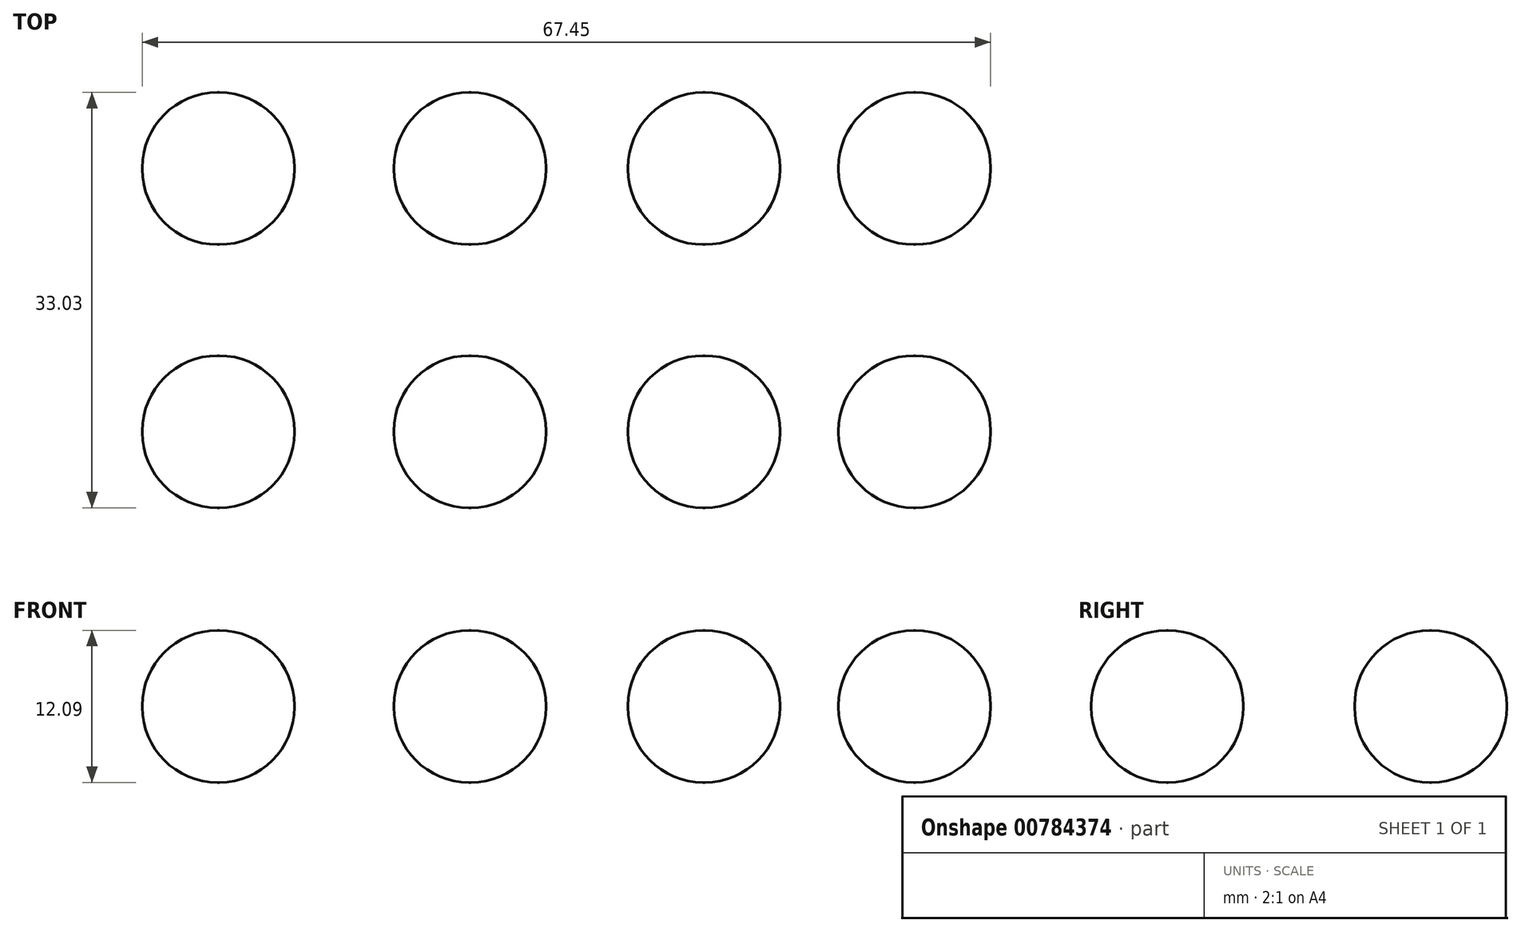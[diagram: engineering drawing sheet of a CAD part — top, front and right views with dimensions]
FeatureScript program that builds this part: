
annotation { "Feature Type Name" : "Feature", "Feature Type Description" : "" }
export const myFeature = defineFeature(function(context is Context, id is Id, definition is map)
    precondition{}
    {
        {
            var Q0;
            Q0=qCreatedBy(makeId("Top.planeOp"),FACE);
            var sketch = newSketch(context, id + "F0", { "sketchPlane" : qUnion([Q0])});
            skLineSegment(sketch, "E0.bottom", {"start": v(-61.29, 39.2) * mm, "end": v(-49.2, 39.2) * mm});
            skLineSegment(sketch, "E0.top", {"start": v(-61.29, 27.1) * mm, "end": v(-49.2, 27.1) * mm});
            skLineSegment(sketch, "E0.left", {"start": v(-61.29, 39.2) * mm, "end": v(-61.29, 27.1) * mm});
            skLineSegment(sketch, "E0.right", {"start": v(-49.2, 39.2) * mm, "end": v(-49.2, 27.1) * mm});
            skLineSegment(sketch, "E1.bottom", {"start": v(-61.29, 18.26) * mm, "end": v(-49.2, 18.26) * mm});
            skLineSegment(sketch, "E1.top", {"start": v(-61.29, 6.16) * mm, "end": v(-49.2, 6.16) * mm});
            skLineSegment(sketch, "E1.left", {"start": v(-61.29, 18.26) * mm, "end": v(-61.29, 6.16) * mm});
            skLineSegment(sketch, "E1.right", {"start": v(-49.2, 18.26) * mm, "end": v(-49.2, 6.16) * mm});
            skLineSegment(sketch, "E2.bottom", {"start": v(-41.28, 39.2) * mm, "end": v(-29.19, 39.2) * mm});
            skLineSegment(sketch, "E2.top", {"start": v(-41.28, 27.1) * mm, "end": v(-29.19, 27.1) * mm});
            skLineSegment(sketch, "E2.left", {"start": v(-41.28, 39.2) * mm, "end": v(-41.28, 27.1) * mm});
            skLineSegment(sketch, "E2.right", {"start": v(-29.19, 39.2) * mm, "end": v(-29.19, 27.1) * mm});
            skLineSegment(sketch, "E3.bottom", {"start": v(-41.28, 18.26) * mm, "end": v(-29.19, 18.26) * mm});
            skLineSegment(sketch, "E3.top", {"start": v(-41.28, 6.16) * mm, "end": v(-29.19, 6.16) * mm});
            skLineSegment(sketch, "E3.left", {"start": v(-41.28, 18.26) * mm, "end": v(-41.28, 6.16) * mm});
            skLineSegment(sketch, "E3.right", {"start": v(-29.19, 18.26) * mm, "end": v(-29.19, 6.16) * mm});
            skLineSegment(sketch, "E4.bottom", {"start": v(-22.68, 39.2) * mm, "end": v(-10.58, 39.2) * mm});
            skLineSegment(sketch, "E4.top", {"start": v(-22.68, 27.1) * mm, "end": v(-10.58, 27.1) * mm});
            skLineSegment(sketch, "E4.left", {"start": v(-22.68, 39.2) * mm, "end": v(-22.68, 27.1) * mm});
            skLineSegment(sketch, "E4.right", {"start": v(-10.58, 39.2) * mm, "end": v(-10.58, 27.1) * mm});
            skLineSegment(sketch, "E5.bottom", {"start": v(-5.93, 39.2) * mm, "end": v(6.16, 39.2) * mm});
            skLineSegment(sketch, "E5.top", {"start": v(-5.93, 27.1) * mm, "end": v(6.16, 27.1) * mm});
            skLineSegment(sketch, "E5.left", {"start": v(-5.93, 39.2) * mm, "end": v(-5.93, 27.1) * mm});
            skLineSegment(sketch, "E5.right", {"start": v(6.16, 39.2) * mm, "end": v(6.16, 27.1) * mm});
            skLineSegment(sketch, "E6.bottom", {"start": v(-22.68, 18.26) * mm, "end": v(-10.58, 18.26) * mm});
            skLineSegment(sketch, "E6.top", {"start": v(-22.68, 6.16) * mm, "end": v(-10.58, 6.16) * mm});
            skLineSegment(sketch, "E6.left", {"start": v(-22.68, 18.26) * mm, "end": v(-22.68, 6.16) * mm});
            skLineSegment(sketch, "E6.right", {"start": v(-10.58, 18.26) * mm, "end": v(-10.58, 6.16) * mm});
            skLineSegment(sketch, "E7.bottom", {"start": v(-5.93, 18.26) * mm, "end": v(6.16, 18.26) * mm});
            skLineSegment(sketch, "E7.top", {"start": v(-5.93, 6.16) * mm, "end": v(6.16, 6.16) * mm});
            skLineSegment(sketch, "E7.left", {"start": v(-5.93, 18.26) * mm, "end": v(-5.93, 6.16) * mm});
            skLineSegment(sketch, "E7.right", {"start": v(6.16, 18.26) * mm, "end": v(6.16, 6.16) * mm});
            skSolve(sketch);
        }
        {
            var Q0;
            Q0 = qSketchRegion(id + "F0", true);
            extrude(context, id + "F1", {"entities" : qUnion([Q0]), "depth" : 12.1 * mm, "offsetDistance" : 25.4 * mm});
        }
        {
            var Q0;
            Q0=makeQuery(id+"F1.opExtrude","CAP_EDGE",EDGE,{"disambiguationData":[OSD([sQuery(id+"F0.wireOp",EDGE,"E0.left")])],"isStart":false});
            var Q1;
            Q1=makeQuery(id+"F1.opExtrude","CAP_EDGE",EDGE,{"disambiguationData":[OSD([sQuery(id+"F0.wireOp",EDGE,"E0.top")])],"isStart":false});
            var Q2;
            Q2=makeQuery(id+"F1.opExtrude","CAP_EDGE",EDGE,{"disambiguationData":[OSD([sQuery(id+"F0.wireOp",EDGE,"E0.bottom")])],"isStart":false});
            var Q3;
            Q3=makeQuery(id+"F1.opExtrude","CAP_EDGE",EDGE,{"disambiguationData":[OSD([sQuery(id+"F0.wireOp",EDGE,"E0.right")])],"isStart":false});
            var Q4;
            Q4=makeQuery(id+"F1.opExtrude","CAP_EDGE",EDGE,{"disambiguationData":[OSD([sQuery(id+"F0.wireOp",EDGE,"E2.left")])],"isStart":false});
            var Q5;
            Q5=makeQuery(id+"F1.opExtrude","CAP_EDGE",EDGE,{"disambiguationData":[OSD([sQuery(id+"F0.wireOp",EDGE,"E2.top")])],"isStart":false});
            var Q6;
            Q6=makeQuery(id+"F1.opExtrude","CAP_EDGE",EDGE,{"disambiguationData":[OSD([sQuery(id+"F0.wireOp",EDGE,"E2.right")])],"isStart":false});
            var Q7;
            Q7=makeQuery(id+"F1.opExtrude","CAP_EDGE",EDGE,{"disambiguationData":[OSD([sQuery(id+"F0.wireOp",EDGE,"E2.bottom")])],"isStart":false});
            var Q8;
            Q8=makeQuery(id+"F1.opExtrude","CAP_EDGE",EDGE,{"disambiguationData":[OSD([sQuery(id+"F0.wireOp",EDGE,"E4.bottom")])],"isStart":false});
            var Q9;
            Q9=makeQuery(id+"F1.opExtrude","CAP_EDGE",EDGE,{"disambiguationData":[OSD([sQuery(id+"F0.wireOp",EDGE,"E4.left")])],"isStart":false});
            var Q10;
            Q10=makeQuery(id+"F1.opExtrude","CAP_EDGE",EDGE,{"disambiguationData":[OSD([sQuery(id+"F0.wireOp",EDGE,"E4.top")])],"isStart":false});
            var Q11;
            Q11=makeQuery(id+"F1.opExtrude","CAP_EDGE",EDGE,{"disambiguationData":[OSD([sQuery(id+"F0.wireOp",EDGE,"E4.right")])],"isStart":false});
            var Q12;
            Q12=makeQuery(id+"F1.opExtrude","CAP_EDGE",EDGE,{"disambiguationData":[OSD([sQuery(id+"F0.wireOp",EDGE,"E5.left")])],"isStart":false});
            var Q13;
            Q13=makeQuery(id+"F1.opExtrude","CAP_EDGE",EDGE,{"disambiguationData":[OSD([sQuery(id+"F0.wireOp",EDGE,"E5.bottom")])],"isStart":false});
            var Q14;
            Q14=makeQuery(id+"F1.opExtrude","CAP_EDGE",EDGE,{"disambiguationData":[OSD([sQuery(id+"F0.wireOp",EDGE,"E5.right")])],"isStart":false});
            var Q15;
            Q15=makeQuery(id+"F1.opExtrude","CAP_EDGE",EDGE,{"disambiguationData":[OSD([sQuery(id+"F0.wireOp",EDGE,"E5.top")])],"isStart":false});
            var Q16;
            Q16=makeQuery(id+"F1.opExtrude","CAP_EDGE",EDGE,{"disambiguationData":[OSD([sQuery(id+"F0.wireOp",EDGE,"E7.bottom")])],"isStart":false});
            var Q17;
            Q17=makeQuery(id+"F1.opExtrude","CAP_EDGE",EDGE,{"disambiguationData":[OSD([sQuery(id+"F0.wireOp",EDGE,"E7.right")])],"isStart":false});
            var Q18;
            Q18=makeQuery(id+"F1.opExtrude","CAP_EDGE",EDGE,{"disambiguationData":[OSD([sQuery(id+"F0.wireOp",EDGE,"E7.top")])],"isStart":false});
            var Q19;
            Q19=makeQuery(id+"F1.opExtrude","CAP_EDGE",EDGE,{"disambiguationData":[OSD([sQuery(id+"F0.wireOp",EDGE,"E7.left")])],"isStart":false});
            var Q20;
            Q20=makeQuery(id+"F1.opExtrude","CAP_EDGE",EDGE,{"disambiguationData":[OSD([sQuery(id+"F0.wireOp",EDGE,"E6.right")])],"isStart":false});
            var Q21;
            Q21=makeQuery(id+"F1.opExtrude","CAP_EDGE",EDGE,{"disambiguationData":[OSD([sQuery(id+"F0.wireOp",EDGE,"E6.top")])],"isStart":false});
            var Q22;
            Q22=makeQuery(id+"F1.opExtrude","CAP_EDGE",EDGE,{"disambiguationData":[OSD([sQuery(id+"F0.wireOp",EDGE,"E6.bottom")])],"isStart":false});
            var Q23;
            Q23=makeQuery(id+"F1.opExtrude","CAP_EDGE",EDGE,{"disambiguationData":[OSD([sQuery(id+"F0.wireOp",EDGE,"E6.left")])],"isStart":false});
            var Q24;
            Q24=makeQuery(id+"F1.opExtrude","CAP_EDGE",EDGE,{"disambiguationData":[OSD([sQuery(id+"F0.wireOp",EDGE,"E3.top")])],"isStart":false});
            var Q25;
            Q25=makeQuery(id+"F1.opExtrude","CAP_EDGE",EDGE,{"disambiguationData":[OSD([sQuery(id+"F0.wireOp",EDGE,"E3.right")])],"isStart":false});
            var Q26;
            Q26=makeQuery(id+"F1.opExtrude","CAP_EDGE",EDGE,{"disambiguationData":[OSD([sQuery(id+"F0.wireOp",EDGE,"E3.bottom")])],"isStart":false});
            var Q27;
            Q27=makeQuery(id+"F1.opExtrude","CAP_EDGE",EDGE,{"disambiguationData":[OSD([sQuery(id+"F0.wireOp",EDGE,"E3.left")])],"isStart":false});
            var Q28;
            Q28=makeQuery(id+"F1.opExtrude","CAP_EDGE",EDGE,{"disambiguationData":[OSD([sQuery(id+"F0.wireOp",EDGE,"E1.right")])],"isStart":false});
            var Q29;
            Q29=makeQuery(id+"F1.opExtrude","CAP_EDGE",EDGE,{"disambiguationData":[OSD([sQuery(id+"F0.wireOp",EDGE,"E1.top")])],"isStart":false});
            var Q30;
            Q30=makeQuery(id+"F1.opExtrude","CAP_EDGE",EDGE,{"disambiguationData":[OSD([sQuery(id+"F0.wireOp",EDGE,"E1.left")])],"isStart":false});
            var Q31;
            Q31=makeQuery(id+"F1.opExtrude","CAP_EDGE",EDGE,{"disambiguationData":[OSD([sQuery(id+"F0.wireOp",EDGE,"E1.bottom")])],"isStart":false});
            var Q32;
            Q32=makeQuery(id+"F1.opExtrude","SWEPT_EDGE",EDGE,{"disambiguationData":[OSD([sQuery(id+"F0.wireOp",EDGE,"E7.top"),sQuery(id+"F0.wireOp",EDGE,"E7.right")])]});
            var Q33;
            Q33=makeQuery(id+"F1.opExtrude","SWEPT_EDGE",EDGE,{"disambiguationData":[OSD([sQuery(id+"F0.wireOp",EDGE,"E7.top"),sQuery(id+"F0.wireOp",EDGE,"E7.left")])]});
            var Q34;
            Q34=makeQuery(id+"F1.opExtrude","SWEPT_EDGE",EDGE,{"disambiguationData":[OSD([sQuery(id+"F0.wireOp",EDGE,"E6.top"),sQuery(id+"F0.wireOp",EDGE,"E6.right")])]});
            var Q35;
            Q35=makeQuery(id+"F1.opExtrude","SWEPT_EDGE",EDGE,{"disambiguationData":[OSD([sQuery(id+"F0.wireOp",EDGE,"E6.top"),sQuery(id+"F0.wireOp",EDGE,"E6.left")])]});
            var Q36;
            Q36=makeQuery(id+"F1.opExtrude","SWEPT_EDGE",EDGE,{"disambiguationData":[OSD([sQuery(id+"F0.wireOp",EDGE,"E3.top"),sQuery(id+"F0.wireOp",EDGE,"E3.right")])]});
            var Q37;
            Q37=makeQuery(id+"F1.opExtrude","SWEPT_EDGE",EDGE,{"disambiguationData":[OSD([sQuery(id+"F0.wireOp",EDGE,"E3.top"),sQuery(id+"F0.wireOp",EDGE,"E3.left")])]});
            var Q38;
            Q38=makeQuery(id+"F1.opExtrude","SWEPT_EDGE",EDGE,{"disambiguationData":[OSD([sQuery(id+"F0.wireOp",EDGE,"E1.top"),sQuery(id+"F0.wireOp",EDGE,"E1.right")])]});
            var Q39;
            Q39=makeQuery(id+"F1.opExtrude","SWEPT_EDGE",EDGE,{"disambiguationData":[OSD([sQuery(id+"F0.wireOp",EDGE,"E1.top"),sQuery(id+"F0.wireOp",EDGE,"E1.left")])]});
            var Q40;
            Q40=makeQuery(id+"F1.opExtrude","CAP_EDGE",EDGE,{"disambiguationData":[OSD([sQuery(id+"F0.wireOp",EDGE,"E7.right")])],"isStart":true});
            var Q41;
            Q41=makeQuery(id+"F1.opExtrude","CAP_EDGE",EDGE,{"disambiguationData":[OSD([sQuery(id+"F0.wireOp",EDGE,"E7.bottom")])],"isStart":true});
            var Q42;
            Q42=makeQuery(id+"F1.opExtrude","CAP_EDGE",EDGE,{"disambiguationData":[OSD([sQuery(id+"F0.wireOp",EDGE,"E7.left")])],"isStart":true});
            var Q43;
            Q43=makeQuery(id+"F1.opExtrude","CAP_EDGE",EDGE,{"disambiguationData":[OSD([sQuery(id+"F0.wireOp",EDGE,"E6.right")])],"isStart":true});
            var Q44;
            Q44=makeQuery(id+"F1.opExtrude","CAP_EDGE",EDGE,{"disambiguationData":[OSD([sQuery(id+"F0.wireOp",EDGE,"E6.left")])],"isStart":true});
            var Q45;
            Q45=makeQuery(id+"F1.opExtrude","CAP_EDGE",EDGE,{"disambiguationData":[OSD([sQuery(id+"F0.wireOp",EDGE,"E6.bottom")])],"isStart":true});
            var Q46;
            Q46=makeQuery(id+"F1.opExtrude","CAP_EDGE",EDGE,{"disambiguationData":[OSD([sQuery(id+"F0.wireOp",EDGE,"E3.right")])],"isStart":true});
            var Q47;
            Q47=makeQuery(id+"F1.opExtrude","CAP_EDGE",EDGE,{"disambiguationData":[OSD([sQuery(id+"F0.wireOp",EDGE,"E3.left")])],"isStart":true});
            var Q48;
            Q48=makeQuery(id+"F1.opExtrude","CAP_EDGE",EDGE,{"disambiguationData":[OSD([sQuery(id+"F0.wireOp",EDGE,"E3.bottom")])],"isStart":true});
            var Q49;
            Q49=makeQuery(id+"F1.opExtrude","CAP_EDGE",EDGE,{"disambiguationData":[OSD([sQuery(id+"F0.wireOp",EDGE,"E1.right")])],"isStart":true});
            var Q50;
            Q50=makeQuery(id+"F1.opExtrude","CAP_EDGE",EDGE,{"disambiguationData":[OSD([sQuery(id+"F0.wireOp",EDGE,"E1.bottom")])],"isStart":true});
            var Q51;
            Q51=makeQuery(id+"F1.opExtrude","CAP_EDGE",EDGE,{"disambiguationData":[OSD([sQuery(id+"F0.wireOp",EDGE,"E1.left")])],"isStart":true});
            var Q52;
            Q52=makeQuery(id+"F1.opExtrude","CAP_EDGE",EDGE,{"disambiguationData":[OSD([sQuery(id+"F0.wireOp",EDGE,"E3.top")])],"isStart":true});
            var Q53;
            Q53=makeQuery(id+"F1.opExtrude","CAP_EDGE",EDGE,{"disambiguationData":[OSD([sQuery(id+"F0.wireOp",EDGE,"E1.top")])],"isStart":true});
            var Q54;
            Q54=makeQuery(id+"F1.opExtrude","CAP_EDGE",EDGE,{"disambiguationData":[OSD([sQuery(id+"F0.wireOp",EDGE,"E6.top")])],"isStart":true});
            var Q55;
            Q55=makeQuery(id+"F1.opExtrude","CAP_EDGE",EDGE,{"disambiguationData":[OSD([sQuery(id+"F0.wireOp",EDGE,"E7.top")])],"isStart":true});
            var Q56;
            Q56=makeQuery(id+"F1.opExtrude","CAP_EDGE",EDGE,{"disambiguationData":[OSD([sQuery(id+"F0.wireOp",EDGE,"E5.top")])],"isStart":true});
            var Q57;
            Q57=makeQuery(id+"F1.opExtrude","CAP_EDGE",EDGE,{"disambiguationData":[OSD([sQuery(id+"F0.wireOp",EDGE,"E5.right")])],"isStart":true});
            var Q58;
            Q58=makeQuery(id+"F1.opExtrude","CAP_EDGE",EDGE,{"disambiguationData":[OSD([sQuery(id+"F0.wireOp",EDGE,"E5.bottom")])],"isStart":true});
            var Q59;
            Q59=makeQuery(id+"F1.opExtrude","CAP_EDGE",EDGE,{"disambiguationData":[OSD([sQuery(id+"F0.wireOp",EDGE,"E5.left")])],"isStart":true});
            var Q60;
            Q60=makeQuery(id+"F1.opExtrude","CAP_EDGE",EDGE,{"disambiguationData":[OSD([sQuery(id+"F0.wireOp",EDGE,"E4.top")])],"isStart":true});
            var Q61;
            Q61=makeQuery(id+"F1.opExtrude","CAP_EDGE",EDGE,{"disambiguationData":[OSD([sQuery(id+"F0.wireOp",EDGE,"E4.right")])],"isStart":true});
            var Q62;
            Q62=makeQuery(id+"F1.opExtrude","CAP_EDGE",EDGE,{"disambiguationData":[OSD([sQuery(id+"F0.wireOp",EDGE,"E4.left")])],"isStart":true});
            var Q63;
            Q63=makeQuery(id+"F1.opExtrude","CAP_EDGE",EDGE,{"disambiguationData":[OSD([sQuery(id+"F0.wireOp",EDGE,"E4.bottom")])],"isStart":true});
            var Q64;
            Q64=makeQuery(id+"F1.opExtrude","CAP_EDGE",EDGE,{"disambiguationData":[OSD([sQuery(id+"F0.wireOp",EDGE,"E2.top")])],"isStart":true});
            var Q65;
            Q65=makeQuery(id+"F1.opExtrude","CAP_EDGE",EDGE,{"disambiguationData":[OSD([sQuery(id+"F0.wireOp",EDGE,"E2.right")])],"isStart":true});
            var Q66;
            Q66=makeQuery(id+"F1.opExtrude","CAP_EDGE",EDGE,{"disambiguationData":[OSD([sQuery(id+"F0.wireOp",EDGE,"E2.left")])],"isStart":true});
            var Q67;
            Q67=makeQuery(id+"F1.opExtrude","CAP_EDGE",EDGE,{"disambiguationData":[OSD([sQuery(id+"F0.wireOp",EDGE,"E2.bottom")])],"isStart":true});
            var Q68;
            Q68=makeQuery(id+"F1.opExtrude","CAP_EDGE",EDGE,{"disambiguationData":[OSD([sQuery(id+"F0.wireOp",EDGE,"E0.bottom")])],"isStart":true});
            var Q69;
            Q69=makeQuery(id+"F1.opExtrude","CAP_EDGE",EDGE,{"disambiguationData":[OSD([sQuery(id+"F0.wireOp",EDGE,"E0.right")])],"isStart":true});
            var Q70;
            Q70=makeQuery(id+"F1.opExtrude","CAP_EDGE",EDGE,{"disambiguationData":[OSD([sQuery(id+"F0.wireOp",EDGE,"E0.top")])],"isStart":true});
            var Q71;
            Q71=makeQuery(id+"F1.opExtrude","CAP_EDGE",EDGE,{"disambiguationData":[OSD([sQuery(id+"F0.wireOp",EDGE,"E0.left")])],"isStart":true});
            var Q72;
            Q72=makeQuery(id+"F1.opExtrude","SWEPT_EDGE",EDGE,{"disambiguationData":[OSD([sQuery(id+"F0.wireOp",EDGE,"E1.bottom"),sQuery(id+"F0.wireOp",EDGE,"E1.left")])]});
            var Q73;
            Q73=makeQuery(id+"F1.opExtrude","SWEPT_EDGE",EDGE,{"disambiguationData":[OSD([sQuery(id+"F0.wireOp",EDGE,"E0.bottom"),sQuery(id+"F0.wireOp",EDGE,"E0.left")])]});
            var Q74;
            Q74=makeQuery(id+"F1.opExtrude","SWEPT_EDGE",EDGE,{"disambiguationData":[OSD([sQuery(id+"F0.wireOp",EDGE,"E0.top"),sQuery(id+"F0.wireOp",EDGE,"E0.left")])]});
            var Q75;
            Q75=makeQuery(id+"F1.opExtrude","SWEPT_EDGE",EDGE,{"disambiguationData":[OSD([sQuery(id+"F0.wireOp",EDGE,"E1.bottom"),sQuery(id+"F0.wireOp",EDGE,"E1.right")])]});
            var Q76;
            Q76=makeQuery(id+"F1.opExtrude","SWEPT_EDGE",EDGE,{"disambiguationData":[OSD([sQuery(id+"F0.wireOp",EDGE,"E0.bottom"),sQuery(id+"F0.wireOp",EDGE,"E0.right")])]});
            var Q77;
            Q77=makeQuery(id+"F1.opExtrude","SWEPT_EDGE",EDGE,{"disambiguationData":[OSD([sQuery(id+"F0.wireOp",EDGE,"E0.top"),sQuery(id+"F0.wireOp",EDGE,"E0.right")])]});
            var Q78;
            Q78=makeQuery(id+"F1.opExtrude","SWEPT_EDGE",EDGE,{"disambiguationData":[OSD([sQuery(id+"F0.wireOp",EDGE,"E3.bottom"),sQuery(id+"F0.wireOp",EDGE,"E3.right")])]});
            var Q79;
            Q79=makeQuery(id+"F1.opExtrude","SWEPT_EDGE",EDGE,{"disambiguationData":[OSD([sQuery(id+"F0.wireOp",EDGE,"E2.bottom"),sQuery(id+"F0.wireOp",EDGE,"E2.right")])]});
            var Q80;
            Q80=makeQuery(id+"F1.opExtrude","SWEPT_EDGE",EDGE,{"disambiguationData":[OSD([sQuery(id+"F0.wireOp",EDGE,"E2.top"),sQuery(id+"F0.wireOp",EDGE,"E2.right")])]});
            var Q81;
            Q81=makeQuery(id+"F1.opExtrude","SWEPT_EDGE",EDGE,{"disambiguationData":[OSD([sQuery(id+"F0.wireOp",EDGE,"E4.top"),sQuery(id+"F0.wireOp",EDGE,"E4.right")])]});
            var Q82;
            Q82=makeQuery(id+"F1.opExtrude","SWEPT_EDGE",EDGE,{"disambiguationData":[OSD([sQuery(id+"F0.wireOp",EDGE,"E4.top"),sQuery(id+"F0.wireOp",EDGE,"E4.left")])]});
            var Q83;
            Q83=makeQuery(id+"F1.opExtrude","SWEPT_EDGE",EDGE,{"disambiguationData":[OSD([sQuery(id+"F0.wireOp",EDGE,"E4.bottom"),sQuery(id+"F0.wireOp",EDGE,"E4.right")])]});
            var Q84;
            Q84=makeQuery(id+"F1.opExtrude","SWEPT_EDGE",EDGE,{"disambiguationData":[OSD([sQuery(id+"F0.wireOp",EDGE,"E4.bottom"),sQuery(id+"F0.wireOp",EDGE,"E4.left")])]});
            var Q85;
            Q85=makeQuery(id+"F1.opExtrude","SWEPT_EDGE",EDGE,{"disambiguationData":[OSD([sQuery(id+"F0.wireOp",EDGE,"E5.top"),sQuery(id+"F0.wireOp",EDGE,"E5.right")])]});
            var Q86;
            Q86=makeQuery(id+"F1.opExtrude","SWEPT_EDGE",EDGE,{"disambiguationData":[OSD([sQuery(id+"F0.wireOp",EDGE,"E5.bottom"),sQuery(id+"F0.wireOp",EDGE,"E5.right")])]});
            var Q87;
            Q87=makeQuery(id+"F1.opExtrude","SWEPT_EDGE",EDGE,{"disambiguationData":[OSD([sQuery(id+"F0.wireOp",EDGE,"E5.bottom"),sQuery(id+"F0.wireOp",EDGE,"E5.left")])]});
            var Q88;
            Q88=makeQuery(id+"F1.opExtrude","SWEPT_EDGE",EDGE,{"disambiguationData":[OSD([sQuery(id+"F0.wireOp",EDGE,"E7.bottom"),sQuery(id+"F0.wireOp",EDGE,"E7.right")])]});
            var Q89;
            Q89=makeQuery(id+"F1.opExtrude","SWEPT_EDGE",EDGE,{"disambiguationData":[OSD([sQuery(id+"F0.wireOp",EDGE,"E7.bottom"),sQuery(id+"F0.wireOp",EDGE,"E7.left")])]});
            var Q90;
            Q90=makeQuery(id+"F1.opExtrude","SWEPT_EDGE",EDGE,{"disambiguationData":[OSD([sQuery(id+"F0.wireOp",EDGE,"E6.bottom"),sQuery(id+"F0.wireOp",EDGE,"E6.right")])]});
            var Q91;
            Q91=makeQuery(id+"F1.opExtrude","SWEPT_EDGE",EDGE,{"disambiguationData":[OSD([sQuery(id+"F0.wireOp",EDGE,"E6.bottom"),sQuery(id+"F0.wireOp",EDGE,"E6.left")])]});
            var Q92;
            Q92=makeQuery(id+"F1.opExtrude","SWEPT_EDGE",EDGE,{"disambiguationData":[OSD([sQuery(id+"F0.wireOp",EDGE,"E3.bottom"),sQuery(id+"F0.wireOp",EDGE,"E3.left")])]});
            var Q93;
            Q93=makeQuery(id+"F1.opExtrude","SWEPT_EDGE",EDGE,{"disambiguationData":[OSD([sQuery(id+"F0.wireOp",EDGE,"E2.bottom"),sQuery(id+"F0.wireOp",EDGE,"E2.left")])]});
            var Q94;
            Q94=makeQuery(id+"F1.opExtrude","SWEPT_FACE",FACE,{"disambiguationData":[OSD([sQuery(id+"F0.wireOp",EDGE,"E5.top")])]});
            var Q95;
            Q95=makeQuery(id+"F1.opExtrude","SWEPT_EDGE",EDGE,{"disambiguationData":[OSD([sQuery(id+"F0.wireOp",EDGE,"E2.top"),sQuery(id+"F0.wireOp",EDGE,"E2.left")])]});
            fillet(context, id + "F2", {"entities" : qUnion([Q0, Q1, Q2, Q3, Q4, Q5, Q6, Q7, Q8, Q9, Q10, Q11, Q12, Q13, Q14, Q15, Q16, Q17, Q18, Q19, Q20, Q21, Q22, Q23, Q24, Q25, Q26, Q27, Q28, Q29, Q30, Q31, Q32, Q33, Q34, Q35, Q36, Q37, Q38, Q39, Q40, Q41, Q42, Q43, Q44, Q45, Q46, Q47, Q48, Q49, Q50, Q51, Q52, Q53, Q54, Q55, Q56, Q57, Q58, Q59, Q60, Q61, Q62, Q63, Q64, Q65, Q66, Q67, Q68, Q69, Q70, Q71, Q72, Q73, Q74, Q75, Q76, Q77, Q78, Q79, Q80, Q81, Q82, Q83, Q84, Q85, Q86, Q87, Q88, Q89, Q90, Q91, Q92, Q93, Q94, Q95]), "radius" : 5.98 * mm, "tangentPropagation" : true, "allowEdgeOverflow" : false});
        }
    });
